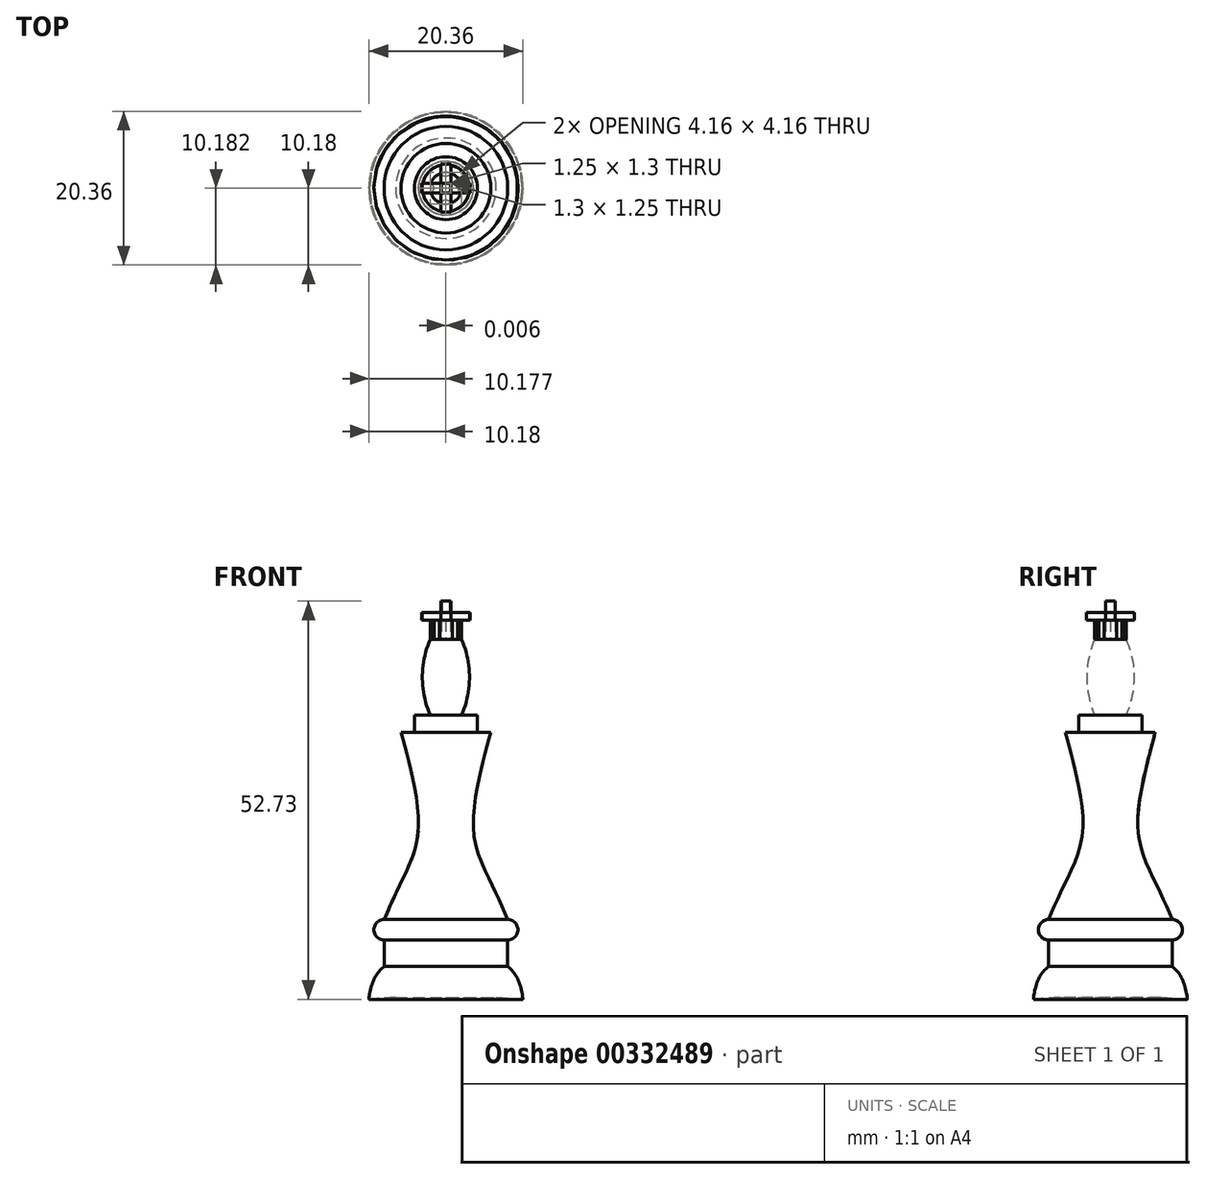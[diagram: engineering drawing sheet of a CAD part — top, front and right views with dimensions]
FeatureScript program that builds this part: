
annotation { "Feature Type Name" : "Feature", "Feature Type Description" : "" }
export const myFeature = defineFeature(function(context is Context, id is Id, definition is map)
    precondition{}
    {
        {
            var Q0;
            Q0=qCreatedBy(makeId("Front.planeOp"),FACE);
            var sketch = newSketch(context, id + "F0", { "sketchPlane" : qUnion([Q0])});
            skLineSegment(sketch, "E0.bottom", {"start": v(0, -33.59) * mm, "end": v(6.64, -33.59) * mm});
            skLineSegment(sketch, "E0.top", {"start": v(0, -29.56) * mm, "end": v(6.64, -29.56) * mm});
            skLineSegment(sketch, "E0.left", {"start": v(0, -33.59) * mm, "end": v(0, -29.56) * mm});
            skLineSegment(sketch, "E0.right", {"start": v(6.64, -33.59) * mm, "end": v(6.64, -29.56) * mm});
            skPoint(sketch, "E1.oppositeSnap0", {"position": v(3.32, -29.56) * mm});
            skLineSegment(sketch, "E1.bottom", {"start": v(0, -29.56) * mm, "end": v(3.32, -29.56) * mm});
            skLineSegment(sketch, "E1.top", {"start": v(0, -26) * mm, "end": v(3.32, -26) * mm});
            skLineSegment(sketch, "E1.left", {"start": v(0, -29.56) * mm, "end": v(0, -26) * mm});
            skLineSegment(sketch, "E2.bottom", {"start": v(0, -26) * mm, "end": v(8.18, -26) * mm});
            skLineSegment(sketch, "E2.top", {"start": v(0, -23.29) * mm, "end": v(8.18, -23.29) * mm});
            skLineSegment(sketch, "E2.left", {"start": v(0, -26) * mm, "end": v(0, -23.29) * mm});
            skLineSegment(sketch, "E2.right", {"start": v(8.18, -26) * mm, "end": v(8.18, -23.29) * mm});
            skArc(sketch, "E3", {"start": v(8.18, -26) * mm, "mid": v(9.54, -24.65) * mm, "end": v(8.18, -23.29) * mm});
            skFitSpline(sketch, "E4", {"points": [v(8.18, -23.29) * mm, v(6.07, -18.6) * mm, v(3.72, -12.09) * mm, v(4.63, -3.61) * mm, v(5.94, 1.48) * mm], "startDerivative": vector(-8.8, 20.24) * mm, "endDerivative": vector(5.56, 20.58) * mm});
            skLineSegment(sketch, "E5", {"start": v(5.94, 1.48) * mm, "end": v(0, 1.48) * mm});
            skLineSegment(sketch, "E6", {"start": v(0, 1.48) * mm, "end": v(0, -23.29) * mm});
            skLineSegment(sketch, "E7", {"start": v(8.18, -26) * mm, "end": v(8.18, -29.49) * mm});
            skLineSegment(sketch, "E8", {"start": v(8.18, -29.49) * mm, "end": v(6.64, -29.56) * mm});
            skFitSpline(sketch, "E9", {"points": [v(8.18, -29.49) * mm, v(9.62, -31.4) * mm, v(10.16, -33.85) * mm, v(10.03, -33.58) * mm], "startDerivative": vector(3.8, -3.47) * mm, "endDerivative": vector(-1.14, 2.93) * mm});
            skLineSegment(sketch, "E10", {"start": v(6.64, -33.59) * mm, "end": v(10.16, -33.85) * mm});
            skLineSegment(sketch, "E11.bottom", {"start": v(4.16, 1.48) * mm, "end": v(0, 1.48) * mm});
            skLineSegment(sketch, "E11.top", {"start": v(4.16, 3.8) * mm, "end": v(0, 3.8) * mm});
            skLineSegment(sketch, "E11.left", {"start": v(4.16, 1.48) * mm, "end": v(4.16, 3.8) * mm});
            skLineSegment(sketch, "E11.right", {"start": v(0, 1.48) * mm, "end": v(0, 3.8) * mm});
            skArc(sketch, "E12", {"start": v(2.08, 3.8) * mm, "mid": v(3.12, 8.8) * mm, "end": v(2.08, 13.8) * mm});
            skPoint(sketch, "E12.endSnap0", {"position": v(2.08, 3.8) * mm});
            skLineSegment(sketch, "E13", {"start": v(2.08, 13.8) * mm, "end": v(0, 13.8) * mm});
            skLineSegment(sketch, "E14", {"start": v(0, 13.8) * mm, "end": v(0, 3.8) * mm});
            skSolve(sketch);
        }
        {
            var Q0;
            Q0 = qSketchRegion(id + "F0", true);
            var Q1;
            Q1=sQuery(id+"F0.wireOp",EDGE,"E6");
            revolve(context, id + "F1", {"entities" : qUnion([Q0]), "axis" : qUnion([Q1]), "revolveType" : RevolveType.FULL});
        }
        {
            var Q0;
            Q0=makeQuery(id+"F1.opRevolve","SWEPT_FACE",FACE,{"disambiguationData":[OSD([sQuery(id+"F0.wireOp",EDGE,"E13")])]});
            var sketch = newSketch(context, id + "F2", { "sketchPlane" : qUnion([Q0])});
            skLineSegment(sketch, "E15.bottom", {"start": v(-0.62, 0.65) * mm, "end": v(0.62, 0.65) * mm});
            skLineSegment(sketch, "E15.top", {"start": v(-0.62, -0.65) * mm, "end": v(0.62, -0.65) * mm});
            skLineSegment(sketch, "E15.left", {"start": v(-0.62, 0.65) * mm, "end": v(-0.62, -0.65) * mm});
            skLineSegment(sketch, "E15.right", {"start": v(0.62, 0.65) * mm, "end": v(0.62, -0.65) * mm});
            skPoint(sketch, "E15.middle", {"position": v(0, 0) * mm});
            skSolve(sketch);
        }
        {
            var Q0;
            Q0 = qSketchRegion(id + "F2", true);
            extrude(context, id + "F3", {"entities" : qUnion([Q0]), "operationType" : NewBodyOperationType.ADD, "depth" : 5.08 * mm});
        }
        {
            var Q0;
            Q0=makeQuery(id+"F3.opExtrude","SWEPT_FACE",FACE,{"disambiguationData":[OSD([sQuery(id+"F2.wireOp",EDGE,"E15.left")])]});
            var sketch = newSketch(context, id + "F4", { "sketchPlane" : qUnion([Q0])});
            skLineSegment(sketch, "E16.bottom", {"start": v(-0.65, 17.4) * mm, "end": v(0.65, 17.4) * mm});
            skLineSegment(sketch, "E16.top", {"start": v(-0.65, 16.34) * mm, "end": v(0.65, 16.34) * mm});
            skLineSegment(sketch, "E16.left", {"start": v(-0.65, 17.4) * mm, "end": v(-0.65, 16.34) * mm});
            skLineSegment(sketch, "E16.right", {"start": v(0.65, 17.4) * mm, "end": v(0.65, 16.34) * mm});
            skLineSegment(sketch, "E17.bottom", {"start": v(0.65, 17.4) * mm, "end": v(-0.65, 17.4) * mm});
            skLineSegment(sketch, "E17.top", {"start": v(0.65, 16.34) * mm, "end": v(-0.65, 16.34) * mm});
            skSolve(sketch);
        }
        {
            var Q0;
            Q0 = qSketchRegion(id + "F4", true);
            extrude(context, id + "F5", {"entities" : qUnion([Q0]), "operationType" : NewBodyOperationType.ADD, "endBound" : BoundingType.SYMMETRIC, "depth" : 2.54 * mm});
        }
        {
            var Q0;
            Q0 = qSketchRegion(id + "F4", true);
            extrude(context, id + "F6", {"entities" : qUnion([Q0]), "operationType" : NewBodyOperationType.ADD, "depth" : 2.54 * mm});
        }
        {
            var Q0;
            Q0=makeQuery(id+"F5.opExtrude","CAP_FACE",FACE,{"disambiguationData":[OSD([sQuery(id+"F4.wireOp",EDGE,"E17.bottom"),sQuery(id+"F4.wireOp",EDGE,"E17.top"),sQuery(id+"F4.wireOp",EDGE,"E16.right"),sQuery(id+"F4.wireOp",EDGE,"E16.left")])],"isStart":true});
            var sketch = newSketch(context, id + "F7", { "sketchPlane" : qUnion([Q0])});
            skLineSegment(sketch, "E18.bottom", {"start": v(-0.65, 17.4) * mm, "end": v(0.65, 17.4) * mm});
            skLineSegment(sketch, "E18.top", {"start": v(-0.65, 16.34) * mm, "end": v(0.65, 16.34) * mm});
            skLineSegment(sketch, "E18.left", {"start": v(-0.65, 17.4) * mm, "end": v(-0.65, 16.34) * mm});
            skLineSegment(sketch, "E18.right", {"start": v(0.65, 17.4) * mm, "end": v(0.65, 16.34) * mm});
            skSolve(sketch);
        }
        {
            var Q0;
            Q0 = qSketchRegion(id + "F7", true);
            extrude(context, id + "F8", {"entities" : qUnion([Q0]), "operationType" : NewBodyOperationType.ADD, "depth" : 2.54 * mm});
        }
        {
            var Q0;
            Q0=makeQuery(id+"F1.opRevolve","SWEPT_FACE",FACE,{"disambiguationData":[OSD([sQuery(id+"F0.wireOp",EDGE,"E13")])]});
            var sketch = newSketch(context, id + "F9", { "sketchPlane" : qUnion([Q0])});
            skArc(sketch, "E19", {"start": v(0.8, 1.92) * mm, "mid": v(-0.02, 2.09) * mm, "end": v(-0.85, 1.9) * mm});
            skLineSegment(sketch, "E20", {"start": v(-0.85, 1.9) * mm, "end": v(0, 1.53) * mm});
            skLineSegment(sketch, "E21", {"start": v(0, 1.53) * mm, "end": v(0.8, 1.92) * mm});
            skLineSegment(sketch, "E22.1.0", {"start": v(-1.53, 0) * mm, "end": v(-1.92, 0.8) * mm});
            skLineSegment(sketch, "E22.2.0", {"start": v(0, -1.53) * mm, "end": v(-0.8, -1.92) * mm});
            skLineSegment(sketch, "E22.3.0", {"start": v(1.53, 0) * mm, "end": v(1.92, -0.8) * mm});
            skPoint(sketch, "E22.center", {"position": v(0, 0) * mm});
            skSolve(sketch);
        }
        {
            var Q0;
            Q0 = qSketchRegion(id + "F9", true);
            extrude(context, id + "F10", {"entities" : qUnion([Q0]), "operationType" : NewBodyOperationType.ADD, "depth" : 2.54 * mm});
        }
        {
            var Q0;
            Q0=makeQuery(id+"F1.opRevolve","SWEPT_BODY",BODY,{"disambiguationData":[OSD([sQuery(id+"F0.wireOp",EDGE,"E0.bottom"),sQuery(id+"F0.wireOp",EDGE,"E0.left"),sQuery(id+"F0.wireOp",EDGE,"E1.left"),sQuery(id+"F0.wireOp",EDGE,"E2.left"),sQuery(id+"F0.wireOp",EDGE,"E3"),sQuery(id+"F0.wireOp",EDGE,"E4"),sQuery(id+"F0.wireOp",EDGE,"E5"),sQuery(id+"F0.wireOp",EDGE,"E6"),sQuery(id+"F0.wireOp",EDGE,"E7"),sQuery(id+"F0.wireOp",EDGE,"E9"),sQuery(id+"F0.wireOp",EDGE,"E10"),sQuery(id+"F0.wireOp",EDGE,"E11.top"),sQuery(id+"F0.wireOp",EDGE,"E11.left"),sQuery(id+"F0.wireOp",EDGE,"E11.right"),sQuery(id+"F0.wireOp",EDGE,"E12"),sQuery(id+"F0.wireOp",EDGE,"E13"),sQuery(id+"F0.wireOp",EDGE,"E14")])]});
            var Q1;
            Q1=makeQuery(id+"F1.opRevolve","SWEPT_FACE",FACE,{"disambiguationData":[OSD([sQuery(id+"F0.wireOp",EDGE,"E12")])]});
            circularPattern(context, id + "F11", {"entities" : qUnion([Q0]), "axis" : qUnion([Q1]), "angle" : 360 * degree, "instanceCount" : 4, "equalSpace" : true});
        }
    });
